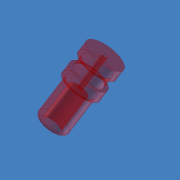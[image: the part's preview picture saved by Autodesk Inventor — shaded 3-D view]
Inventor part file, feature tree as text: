
AUTODESK INVENTOR PART (.ipt)
format: ipt  version: 2013 (Build 170138000, 138)  size: 109,568 bytes
history: native  units: mm
features: hole x2, other x1, fillet x1, sketch x1
ambient origin geometry x8: Origin, YZ Plane, XZ Plane, XY Plane, X Axis, Y Axis, Z Axis, Center Point
bodies: Volumenkörper1 (feature_tree)
feature tree (5):
  other  "Drehung1"
  hole  "Bohrung1"  [1 undecoded]
  hole  "Bohrung2"  [1 undecoded]
  fillet  "Rundung1"  Radius=0.3mm
  sketch  "Skizze1"  dims[d1=2.0mm d6=0.3mm d7=0.3mm d8=0.3mm d9=90.0deg d10=0.5mm d11=0.4mm d13=10.0mm d14=10.0mm d15=0.15mm d16=6.0mm d17=4.0mm d18=2.0mm d19=90.0deg d20=8.0mm d21=0.0mm d22=10.0mm d23=10.0mm d24=0.5mm d25=6.0mm d26=4.0mm d27=2.0mm d28=90.0deg d29=1.0mm d30=0.0mm d31=0.1mm]
note: 2 required parameter values undecoded (feature->parameter linkage not recoverable at this tier; creation-order binding heuristic only, values carry confidence <= 0.55)
